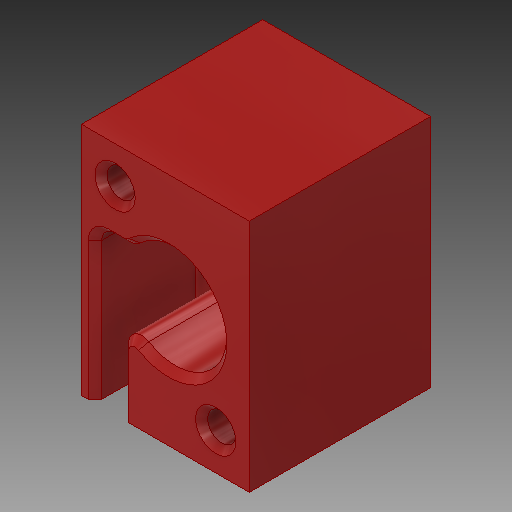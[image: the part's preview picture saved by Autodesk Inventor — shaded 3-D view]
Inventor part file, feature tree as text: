
AUTODESK INVENTOR PART (.ipt)
format: ipt  version: 2019 (Build 230136000, 136)  size: 183,296 bytes
history: native  units: mm
features: sketch x4, extrude x3, fillet x1, hole x1, chamfer x1, projected_geometry x1
ambient origin geometry x8: Origin, YZ Plane, XZ Plane, XY Plane, X Axis, Y Axis, Z Axis, Center Point
bodies: Solid1 (feature_tree)
feature tree (11):
  extrude  "Extrusion1"  Depth=35.0mm
  extrude  "Extrusion2"  Depth=12.0mm
  extrude  "Extrusion3"  Depth=10.0mm
  fillet  "Fillet1"  Radius=11.0mm
  hole  "Hole1"  [1 undecoded]
  chamfer  "Chamfer1"  Distance=15.0mm
  sketch  "Sketch1"  dims[d0=25.0mm d1=35.0mm]
  sketch  "Sketch2"  dims[d2=12.0mm d3=0.0mm d4=6.1mm]
  sketch  "Sketch4"  dims[d5=10.0mm d6=0.0mm d9=15.3mm d10=11.0mm]
  projected_geometry  "Projected Loop2"
  sketch  "Sketch5"  dims[d11=7.0mm d12=5.0mm d13=15.0mm d14=0.0mm d15=2.0mm d16=12.0mm d17=7.0mm d18=12.0mm d19=12.0mm d20=8.0mm d21=4.2mm d22=3.2mm d23=6.0mm d24=2.0mm d25=90.0deg d26=8.0mm d27=20.594885mm d28=1.0mm d29=2.0mm d30=45.0deg]
note: 1 required parameter value undecoded (feature->parameter linkage not recoverable at this tier; creation-order binding heuristic only, values carry confidence <= 0.55)
